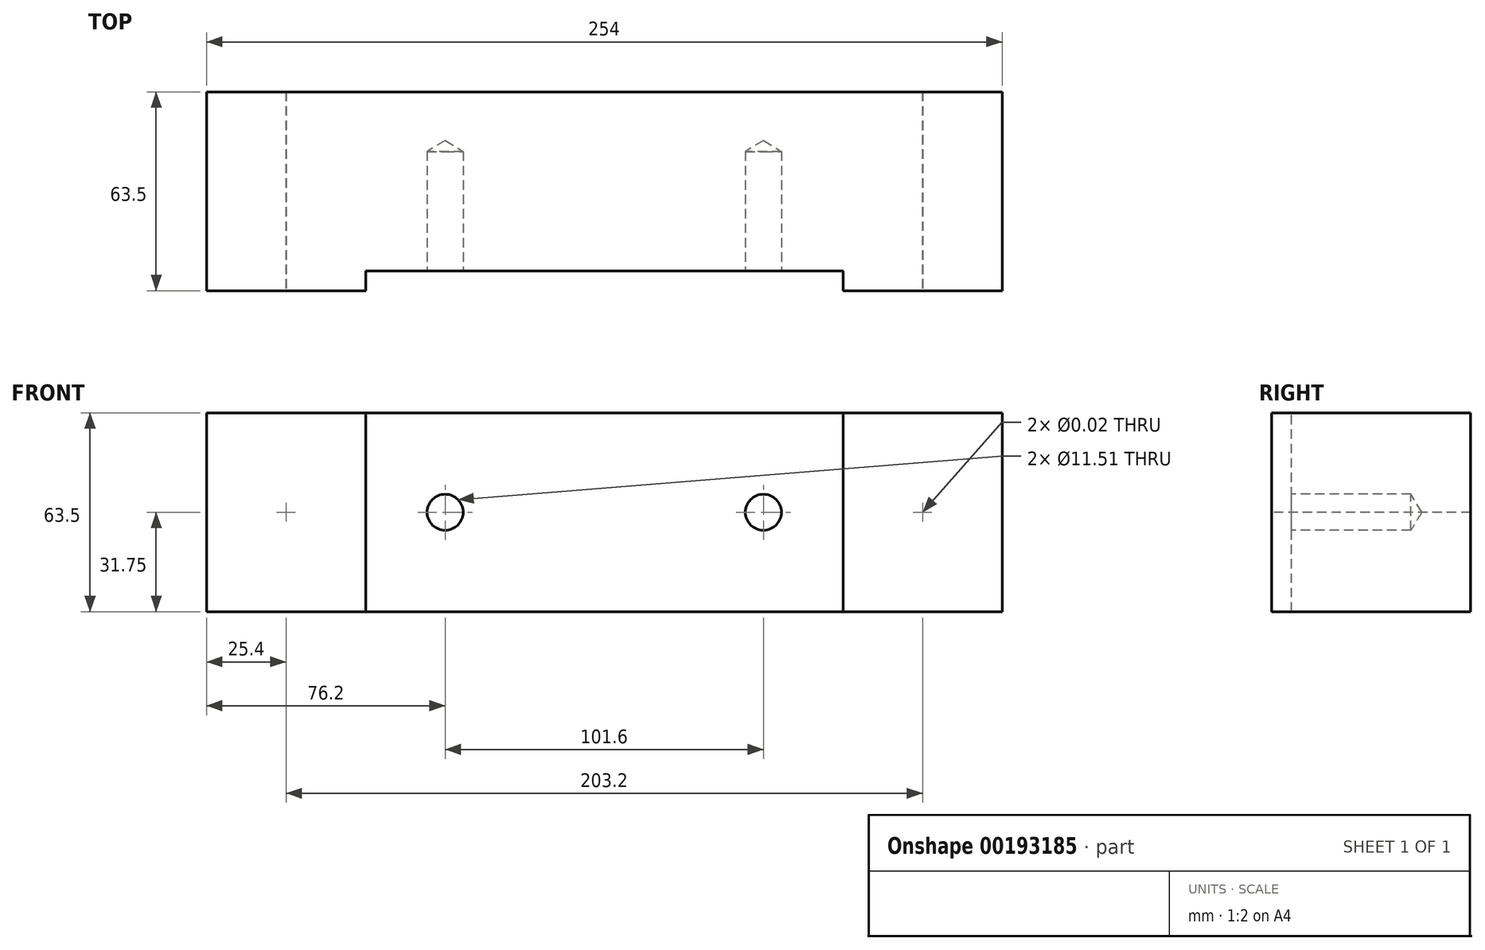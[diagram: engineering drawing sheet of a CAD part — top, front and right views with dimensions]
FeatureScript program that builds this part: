
annotation { "Feature Type Name" : "Feature", "Feature Type Description" : "" }
export const myFeature = defineFeature(function(context is Context, id is Id, definition is map)
    precondition{}
    {
        {
            var Q0;
            Q0=qCreatedBy(makeId("Right.planeOp"),FACE);
            var sketch = newSketch(context, id + "F0", { "sketchPlane" : qUnion([Q0])});
            skLineSegment(sketch, "E0.bottom", {"start": v(-31.75, 31.75) * mm, "end": v(31.75, 31.75) * mm});
            skLineSegment(sketch, "E0.top", {"start": v(-31.75, -31.75) * mm, "end": v(31.75, -31.75) * mm});
            skLineSegment(sketch, "E0.left", {"start": v(-31.75, 31.75) * mm, "end": v(-31.75, -31.75) * mm});
            skLineSegment(sketch, "E0.right", {"start": v(31.75, 31.75) * mm, "end": v(31.75, -31.75) * mm});
            skPoint(sketch, "E0.middle", {"position": v(0, 0) * mm});
            skSolve(sketch);
        }
        {
            var Q0;
            Q0 = qSketchRegion(id + "F0", true);
            extrude(context, id + "F1", {"entities" : qUnion([Q0]), "endBound" : BoundingType.SYMMETRIC, "depth" : 254 * mm});
        }
        {
            var Q0;
            Q0=makeQuery(id+"F1.opExtrude","SWEPT_FACE",FACE,{"disambiguationData":[OSD([sQuery(id+"F0.wireOp",EDGE,"E0.left")])]});
            var sketch = newSketch(context, id + "F2", { "sketchPlane" : qUnion([Q0])});
            skLineSegment(sketch, "E1", {"start": v(-141.57, 0) * mm, "end": v(139.86, 0) * mm, "construction": true});
            skLineSegment(sketch, "E2", {"start": v(0, 104.42) * mm, "end": v(0, -70.87) * mm, "construction": true});
            skLineSegment(sketch, "E3.0", {"start": v(-101.6, 104.42) * mm, "end": v(-101.6, -70.87) * mm, "construction": true});
            skPoint(sketch, "E4", {"position": v(-101.6, 0) * mm});
            skPoint(sketch, "E5.MirrorP", {"position": v(101.6, 0) * mm});
            skSolve(sketch);
        }
        {
            var Q0;
            Q0=sQuery(id+"F2.wireOp",VERTEX,"E4");
            var Q1;
            Q1=sQuery(id+"F2.wireOp",VERTEX,"E5.MirrorP");
            var Q2;
            Q2=makeQuery(id+"F1.opExtrude","SWEPT_BODY",BODY,{"disambiguationData":[OSD([sQuery(id+"F0.wireOp",EDGE,"E0.bottom"),sQuery(id+"F0.wireOp",EDGE,"E0.top"),sQuery(id+"F0.wireOp",EDGE,"E0.left"),sQuery(id+"F0.wireOp",EDGE,"E0.right")])]});
            hole(context, id + "F3", {"style" : HoleStyle.SIMPLE, "endStyle" : HoleEndStyle.THROUGH, "standardTappedOrClearance" : lookupTablePath({ "standard" : "ANSI", "size" : "9/16 (0.56)", "type" : "Drilled" }), "standardBlindInLast" : lookupTablePath({ "standard" : "ANSI", "size" : "9/16", "type" : "Drilled" }), "holeDiameter" : 9 / 406.4 * mm, "locations" : qUnion([Q0, Q1]), "scope" : qUnion([Q2]), "isTappedThrough" : true});
        }
        {
            var Q0;
            Q0=makeQuery(id+"F1.opExtrude","SWEPT_FACE",FACE,{"disambiguationData":[OSD([sQuery(id+"F0.wireOp",EDGE,"E0.left")])]});
            var sketch = newSketch(context, id + "F4", { "sketchPlane" : qUnion([Q0])});
            skLineSegment(sketch, "E6.0", {"start": v(127, 31.75) * mm, "end": v(-127, 31.75) * mm});
            skLineSegment(sketch, "E7.0", {"start": v(127, -31.75) * mm, "end": v(-127, -31.75) * mm});
            skLineSegment(sketch, "E8", {"start": v(0, 93.47) * mm, "end": v(0, -79.77) * mm, "construction": true});
            skLineSegment(sketch, "E9.0", {"start": v(-76.2, 93.47) * mm, "end": v(-76.2, -79.77) * mm, "construction": true});
            skLineSegment(sketch, "E10.bottom", {"start": v(-76.2, -31.75) * mm, "end": v(76.2, -31.75) * mm});
            skLineSegment(sketch, "E10.top", {"start": v(-76.2, 31.75) * mm, "end": v(76.2, 31.75) * mm});
            skLineSegment(sketch, "E10.left", {"start": v(-76.2, -31.75) * mm, "end": v(-76.2, 31.75) * mm});
            skLineSegment(sketch, "E10.right", {"start": v(76.2, -31.75) * mm, "end": v(76.2, 31.75) * mm});
            skSolve(sketch);
        }
        {
            var Q0;
            Q0 = qSketchRegion(id + "F4", true);
            extrude(context, id + "F5", {"entities" : qUnion([Q0]), "operationType" : NewBodyOperationType.REMOVE, "oppositeDirection" : true, "depth" : 6.35 * mm});
        }
        {
            var Q0;
            Q0=makeQuery(id+"F5.boolean.opBoolean","COPY",FACE,{"derivedFrom":makeQuery(id+"F5.opExtrude","CAP_FACE",FACE,{"disambiguationData":[OSD([sQuery(id+"F4.wireOp",EDGE,"E10.bottom"),sQuery(id+"F4.wireOp",EDGE,"E10.top"),sQuery(id+"F4.wireOp",EDGE,"E10.left"),sQuery(id+"F4.wireOp",EDGE,"E10.right")])],"isStart":false})});
            var sketch = newSketch(context, id + "F6", { "sketchPlane" : qUnion([Q0])});
            skLineSegment(sketch, "E11", {"start": v(-132.67, 0) * mm, "end": v(146.02, 0) * mm, "construction": true});
            skLineSegment(sketch, "E12", {"start": v(0, 66.08) * mm, "end": v(0, -77.03) * mm, "construction": true});
            skLineSegment(sketch, "E13.0", {"start": v(-50.8, 66.08) * mm, "end": v(-50.8, -77.03) * mm, "construction": true});
            skPoint(sketch, "E14", {"position": v(-50.8, 0) * mm});
            skPoint(sketch, "E15.MirrorP", {"position": v(50.8, 0) * mm});
            skSolve(sketch);
        }
        {
            var Q0;
            Q0=sQuery(id+"F6.wireOp",VERTEX,"E14");
            var Q1;
            Q1=sQuery(id+"F6.wireOp",VERTEX,"E15.MirrorP");
            var Q2;
            Q2=makeQuery(id+"F1.opExtrude","SWEPT_BODY",BODY,{"disambiguationData":[OSD([sQuery(id+"F0.wireOp",EDGE,"E0.bottom"),sQuery(id+"F0.wireOp",EDGE,"E0.top"),sQuery(id+"F0.wireOp",EDGE,"E0.left"),sQuery(id+"F0.wireOp",EDGE,"E0.right")])]});
            hole(context, id + "F7", {"style" : HoleStyle.SIMPLE, "endStyle" : HoleEndStyle.BLIND, "standardTappedOrClearance" : lookupTablePath({ "standard" : "ANSI", "engagement" : "75%", "pitch" : "20 tpi", "size" : "1/2", "type" : "Tapped" }), "standardBlindInLast" : lookupTablePath({ "standard" : "ANSI", "engagement" : "75%", "pitch" : "20 tpi", "size" : "1/2", "type" : "Tapped" }), "holeDiameter" : 11.5 * mm, "holeDepth" : 38.1 * mm, "locations" : qUnion([Q0, Q1]), "scope" : qUnion([Q2]), "majorDiameter" : 12.7 * mm});
        }
    });
